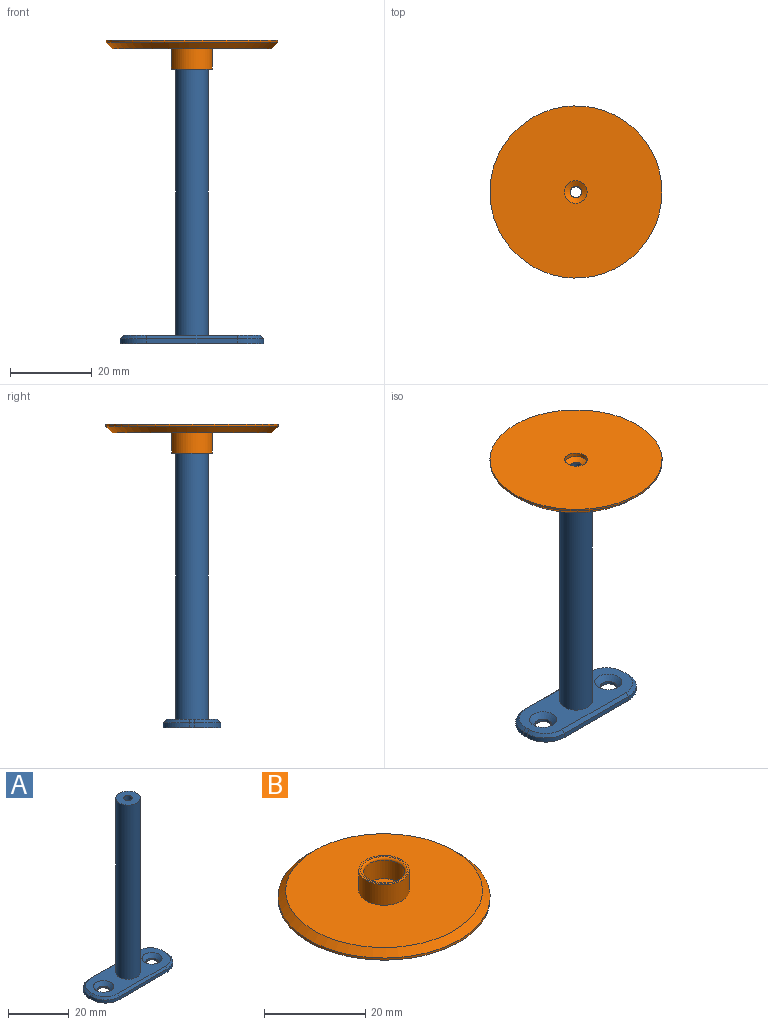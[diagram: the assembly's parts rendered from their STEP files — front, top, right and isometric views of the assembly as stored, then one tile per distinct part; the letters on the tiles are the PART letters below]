
ASSEMBLY  parts=2 mates=1
PART A: 25 faces, bbox 35x14x72 mm
  f0: plane 1.2x1.2mm, normal (1,0,0), area 1.4mm2, adj f5,f10,f13,f17
  f1: plane 22.2x1.2mm, normal (0,1,0), area 26.6mm2, adj f5,f10,f11,f14
  f2: plane 1.2x1.2mm, normal (-1,0,0), area 1.4mm2, adj f5,f11,f12,f18
  f3: plane 22.2x1.2mm, normal (0,-1,0), area 26.6mm2, adj f5,f12,f13,f21
  f4: plane 33.4x12.4mm, normal (0,0,1), area 268.6mm2, adj f8,f9,f14,f15,f16,f17,f18,f19
  f5: plane 35x14mm, normal (0,0,-1), area 423.5mm2, adj f0,f1,f2,f3,f6,f7,f10,f11
  f6: cylinder r=2mm len=4mm, axis (0,0,1), area 8.8mm2, adj f5,f8
  f7: cylinder r=2mm len=4mm, axis (0,0,1), area 8.8mm2, adj f5,f9
  f8: cone r=2mm half-angle=45deg, axis (0,0,1), area 30.6mm2, adj f4,f6
  f9: cone r=2mm half-angle=45deg, axis (0,0,1), area 30.6mm2, adj f4,f7
  f10: cylinder r=6.4mm len=6.4mm, axis (0,0,1), area 12.1mm2, adj f0,f1,f5,f15
  f11: cylinder r=6.4mm len=6.4mm, axis (0,0,-1), area 12.1mm2, adj f1,f2,f5,f16
  f12: cylinder r=6.4mm len=6.4mm, axis (0,0,1), area 12.1mm2, adj f2,f3,f5,f20
  f13: cylinder r=6.4mm len=6.4mm, axis (0,0,-1), area 12.1mm2, adj f0,f3,f5,f19
  f14: plane 22.2x0.8mm, normal (0,0.71,0.71), area 25.1mm2, adj f1,f4,f15,f16
  f15: cone r=5.6mm half-angle=45deg, axis (0,0,-1), area 10.7mm2, adj f4,f10,f14,f17
  f16: cone r=5.6mm half-angle=45deg, axis (0,0,-1), area 10.7mm2, adj f4,f11,f14,f18
  f17: plane 1.2x0.8mm, normal (0.71,0,0.71), area 1.4mm2, adj f0,f4,f15,f19
  f18: plane 1.2x0.8mm, normal (-0.71,0,0.71), area 1.4mm2, adj f2,f4,f16,f20
  f19: cone r=5.6mm half-angle=45deg, axis (0,0,-1), area 10.7mm2, adj f4,f13,f17,f21
  f20: cone r=5.6mm half-angle=45deg, axis (0,0,-1), area 10.7mm2, adj f4,f12,f18,f21
  f21: plane 22.2x0.8mm, normal (0,-0.71,0.71), area 25.1mm2, adj f3,f4,f19,f20
  f22: cylinder r=4mm len=70mm, axis (0,0,-1), area 1759.3mm2, adj f4,f23
  f23: plane 8x8mm, normal (0,0,1), area 44.1mm2, adj f22,f24
  f24: cylinder r=1.4mm len=72mm, axis (0,0,1), area 633.3mm2, adj f5,f23
PART B: 12 faces, bbox 42x42x7 mm
  f0: cone r=0mm half-angle=59deg, axis (0,0,-1), area 20.5mm2, adj f8,f9
  f1: cylinder r=21mm len=42mm, axis (0,0,-1), area 66mm2, adj f3,f10
  f2: plane 39x39mm, normal (0,0,1), area 1116.1mm2, adj f5,f10
  f3: plane 42x42mm, normal (0,0,-1), area 1361.7mm2, adj f1,f8
  f4: cylinder r=4.1mm len=8.2mm, axis (0,0,-1), area 115.9mm2, adj f7,f11
  f5: cylinder r=5mm len=10mm, axis (0,0,-1), area 157.1mm2, adj f2,f6
  f6: plane 10x10mm, normal (0,0,1), area 12.1mm2, adj f5,f11
  f7: plane 8.2x8.2mm, normal (0,0,1), area 46.7mm2, adj f4,f9
  f8: cylinder r=2.75mm len=5.5mm, axis (0,0,-1), area 17.3mm2, adj f0,f3
  f9: cylinder r=1.4mm len=2.8mm, axis (0,0,-1), area 1.7mm2, adj f0,f7
  f10: cone r=19.5mm half-angle=45deg, axis (0,0,-1), area 269.9mm2, adj f1,f2
  f11: torus R=4.6mm, axis (0,0,1), area 21.1mm2, adj f4,f6
PLACE A t=(10.49,53.2,-13.95)mm
PLACE B rot(axis=(1,0,0),180deg) t=(10.4,54.95,60.05)mm
MATE planar A.f22 <-> B.f0  axis (0,0,1) through (10.4,54.95,58.05)mm
